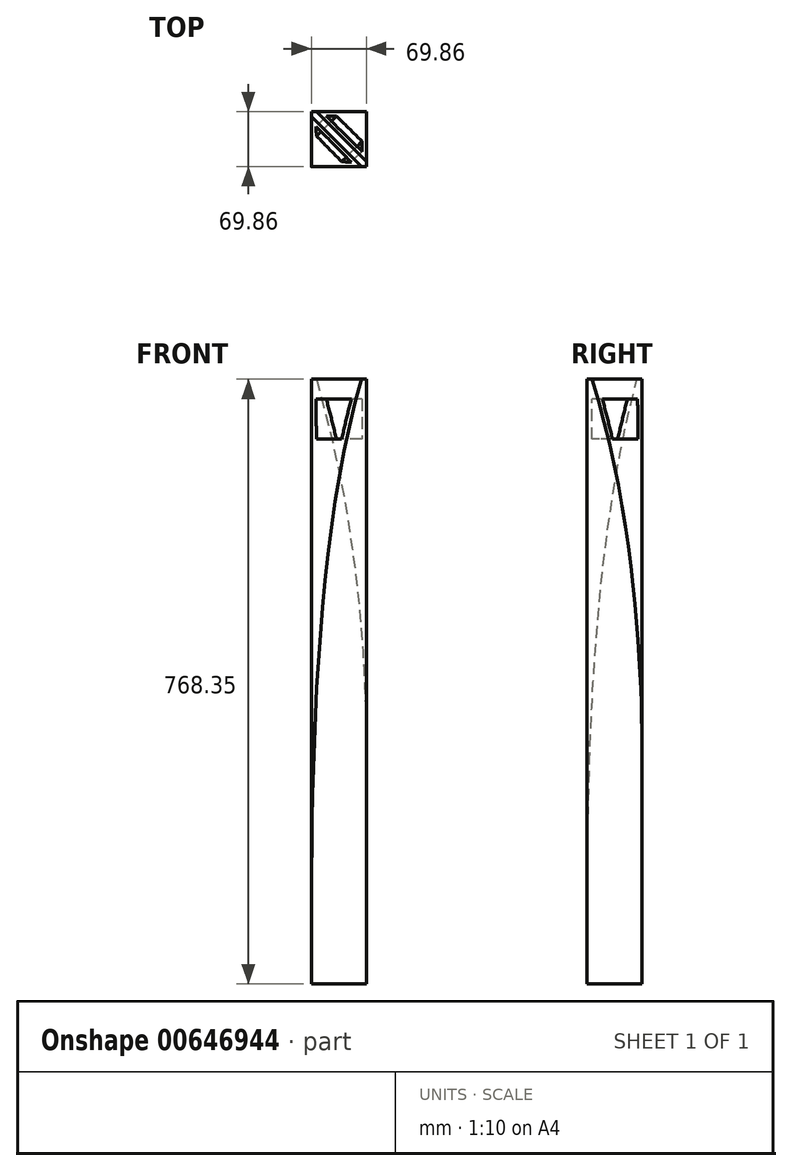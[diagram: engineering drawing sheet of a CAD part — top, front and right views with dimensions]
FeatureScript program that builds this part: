
annotation { "Feature Type Name" : "Feature", "Feature Type Description" : "" }
export const myFeature = defineFeature(function(context is Context, id is Id, definition is map)
    precondition{}
    {
        {
            var Q0;
            Q0=qCreatedBy(makeId("Top.planeOp"),FACE);
            var sketch = newSketch(context, id + "F0", { "sketchPlane" : qUnion([Q0])});
            skLineSegment(sketch, "E0.bottom", {"start": v(34.92, 34.93) * mm, "end": v(-34.93, 34.93) * mm});
            skLineSegment(sketch, "E0.top", {"start": v(34.93, -34.93) * mm, "end": v(-34.92, -34.93) * mm});
            skLineSegment(sketch, "E0.left", {"start": v(34.92, 34.93) * mm, "end": v(34.93, -34.93) * mm});
            skLineSegment(sketch, "E0.right", {"start": v(-34.93, 34.93) * mm, "end": v(-34.93, -34.93) * mm});
            skPoint(sketch, "E0.middle", {"position": v(0, 0) * mm});
            skSolve(sketch);
        }
        {
            var Q0;
            Q0=makeQuery(id+"F0.imprint","IMPRINT",FACE,{"disambiguationData":[TD([[makeQuery(id+"F0.imprint","IMPRINT",EDGE,{"derivedFrom":sQuery(id+"F0.wireOp",EDGE,"E0.bottom")}),1.0]])]});
            extrude(context, id + "F1", {"entities" : qUnion([Q0]), "depth" : 768.35 * mm, "offsetDistance" : 25.4 * mm});
        }
        {
            var Q0;
            Q0=makeQuery(id+"F1.opExtrude","SWEPT_FACE",FACE,{"disambiguationData":[OSD([sQuery(id+"F0.wireOp",EDGE,"E0.left")])]});
            var sketch = newSketch(context, id + "F2", { "sketchPlane" : qUnion([Q0])});
            skPoint(sketch, "E1", {"position": v(34.92, 268.58) * mm});
            skPoint(sketch, "E2", {"position": v(-28.58, 768.35) * mm});
            skFitSpline(sketch, "E3", {"points": [v(-28.58, 768.35) * mm, v(34.92, 268.58) * mm], "startDerivative": vector(190.5, -624.47) * mm, "endDerivative": vector(0, -243.7) * mm});
            skLineSegment(sketch, "E4", {"start": v(-28.58, 768.35) * mm, "end": v(34.92, 768.35) * mm});
            skLineSegment(sketch, "E5", {"start": v(34.92, 768.35) * mm, "end": v(34.93, 349.8) * mm});
            skLineSegment(sketch, "E6", {"start": v(34.92, 268.58) * mm, "end": v(-34.93, 268.58) * mm});
            skSolve(sketch);
        }
        {
            var Q0;
            Q0=makeQuery(id+"F1.opExtrude","CAP_FACE",FACE,{"disambiguationData":[OSD([sQuery(id+"F0.wireOp",EDGE,"E0.bottom"),sQuery(id+"F0.wireOp",EDGE,"E0.top"),sQuery(id+"F0.wireOp",EDGE,"E0.left"),sQuery(id+"F0.wireOp",EDGE,"E0.right")])],"isStart":false});
            var sketch = newSketch(context, id + "F3", { "sketchPlane" : qUnion([Q0])});
            skLineSegment(sketch, "E7", {"start": v(34.93, -28.58) * mm, "end": v(-28.58, 34.93) * mm});
            skLineSegment(sketch, "E8", {"start": v(-28.58, 34.93) * mm, "end": v(34.92, 34.93) * mm});
            skLineSegment(sketch, "E9", {"start": v(34.92, 34.92) * mm, "end": v(34.93, -28.58) * mm});
            skSolve(sketch);
        }
        {
            var Q0;
            Q0=makeQuery(id+"F3.imprint","IMPRINT",FACE,{"disambiguationData":[TD([[makeQuery(id+"F3.imprint","IMPRINT",EDGE,{"derivedFrom":sQuery(id+"F3.wireOp",EDGE,"E7")}),-1.0]])]});
            var Q1;
            Q1=sQuery(id+"F2.wireOp",EDGE,"E3");
            sweep(context, id + "F4", {"operationType" : NewBodyOperationType.REMOVE, "profiles" : qUnion([Q0]), "path" : qUnion([Q1])});
        }
        {
            var Q0;
            Q0=makeQuery(id+"F1.opExtrude","SWEPT_FACE",FACE,{"disambiguationData":[OSD([sQuery(id+"F0.wireOp",EDGE,"E0.top")])]});
            var sketch = newSketch(context, id + "F5", { "sketchPlane" : qUnion([Q0])});
            skLineSegment(sketch, "E10", {"start": v(-34.93, 25.86) * mm, "end": v(34.93, 25.86) * mm});
            skPoint(sketch, "E11", {"position": v(28.58, 768.35) * mm});
            skFitSpline(sketch, "E12", {"points": [v(28.58, 768.35) * mm, v(-34.93, 25.86) * mm], "startDerivative": vector(-190.5, -670.57) * mm, "endDerivative": vector(0, -636.81) * mm});
            skSolve(sketch);
        }
        {
            var Q0;
            Q0=makeQuery(id+"F1.opExtrude","CAP_FACE",FACE,{"disambiguationData":[OSD([sQuery(id+"F0.wireOp",EDGE,"E0.bottom"),sQuery(id+"F0.wireOp",EDGE,"E0.top"),sQuery(id+"F0.wireOp",EDGE,"E0.left"),sQuery(id+"F0.wireOp",EDGE,"E0.right")])],"isStart":false});
            var sketch = newSketch(context, id + "F6", { "sketchPlane" : qUnion([Q0])});
            skLineSegment(sketch, "E13", {"start": v(-34.92, 28.58) * mm, "end": v(28.58, -34.92) * mm});
            skSolve(sketch);
        }
        {
            var Q0;
            {var subQ0=sQuery(id+"F6.wireOp",EDGE,"E13");Q0=makeQuery(id+"F6.imprint","IMPRINT",FACE,{"disambiguationData":[TD([[makeQuery(id+"F6.imprint","IMPRINT",EDGE,{"derivedFrom":subQ0}),-1.0]])]});}
            var Q1;
            Q1=sQuery(id+"F5.wireOp",EDGE,"E12");
            sweep(context, id + "F7", {"operationType" : NewBodyOperationType.REMOVE, "profiles" : qUnion([Q0]), "path" : qUnion([Q1])});
        }
        {
            var Q0;
            Q0=makeQuery(id+"F1.opExtrude","SWEPT_EDGE",EDGE,{"disambiguationData":[OSD([sQuery(id+"F0.wireOp",EDGE,"E0.top"),sQuery(id+"F0.wireOp",EDGE,"E0.left")])]});
            cPlane(context, id + "F8", {"entities" : qUnion([Q0]), "cplaneType" : CPlaneType.LINE_ANGLE, "offset" : 25.4 * mm, "angle" : 45 * degree, "oppositeDirection" : true, "width" : 152.4 * mm, "height" : 152.4 * mm});
        }
        {
            var Q0;
            Q0=qCreatedBy(id+"F8.planeOp",FACE);
            var sketch = newSketch(context, id + "F9", { "sketchPlane" : qUnion([Q0])});
            skPoint(sketch, "E14", {"position": v(31.75, 742.95) * mm});
            skPoint(sketch, "E15", {"position": v(-31.75, 742.95) * mm});
            skPoint(sketch, "E16", {"position": v(22.8, 692.15) * mm});
            skPoint(sketch, "E17", {"position": v(-22.8, 692.15) * mm});
            skLineSegment(sketch, "E18", {"start": v(31.75, 742.95) * mm, "end": v(-31.75, 742.95) * mm});
            skLineSegment(sketch, "E19", {"start": v(-22.8, 692.15) * mm, "end": v(-31.75, 742.95) * mm});
            skLineSegment(sketch, "E20", {"start": v(22.8, 692.15) * mm, "end": v(-22.8, 692.15) * mm});
            skLineSegment(sketch, "E21", {"start": v(0, 742.95) * mm, "end": v(0, 768.35) * mm, "construction": true});
            skLineSegment(sketch, "E22.0", {"start": v(44.9, 768.35) * mm, "end": v(-44.9, 768.35) * mm, "construction": true});
            skPoint(sketch, "E23.0", {"position": v(0, 268.58) * mm});
            skLineSegment(sketch, "E24", {"start": v(31.75, 742.95) * mm, "end": v(22.8, 692.15) * mm});
            skSolve(sketch);
        }
        {
            var Q0;
            Q0 = qSketchRegion(id + "F9", true);
            extrude(context, id + "F10", {"entities" : qUnion([Q0]), "operationType" : NewBodyOperationType.REMOVE, "endBound" : BoundingType.SYMMETRIC, "oppositeDirection" : true, "depth" : 254 * mm, "offsetDistance" : 25.4 * mm});
        }
    });
